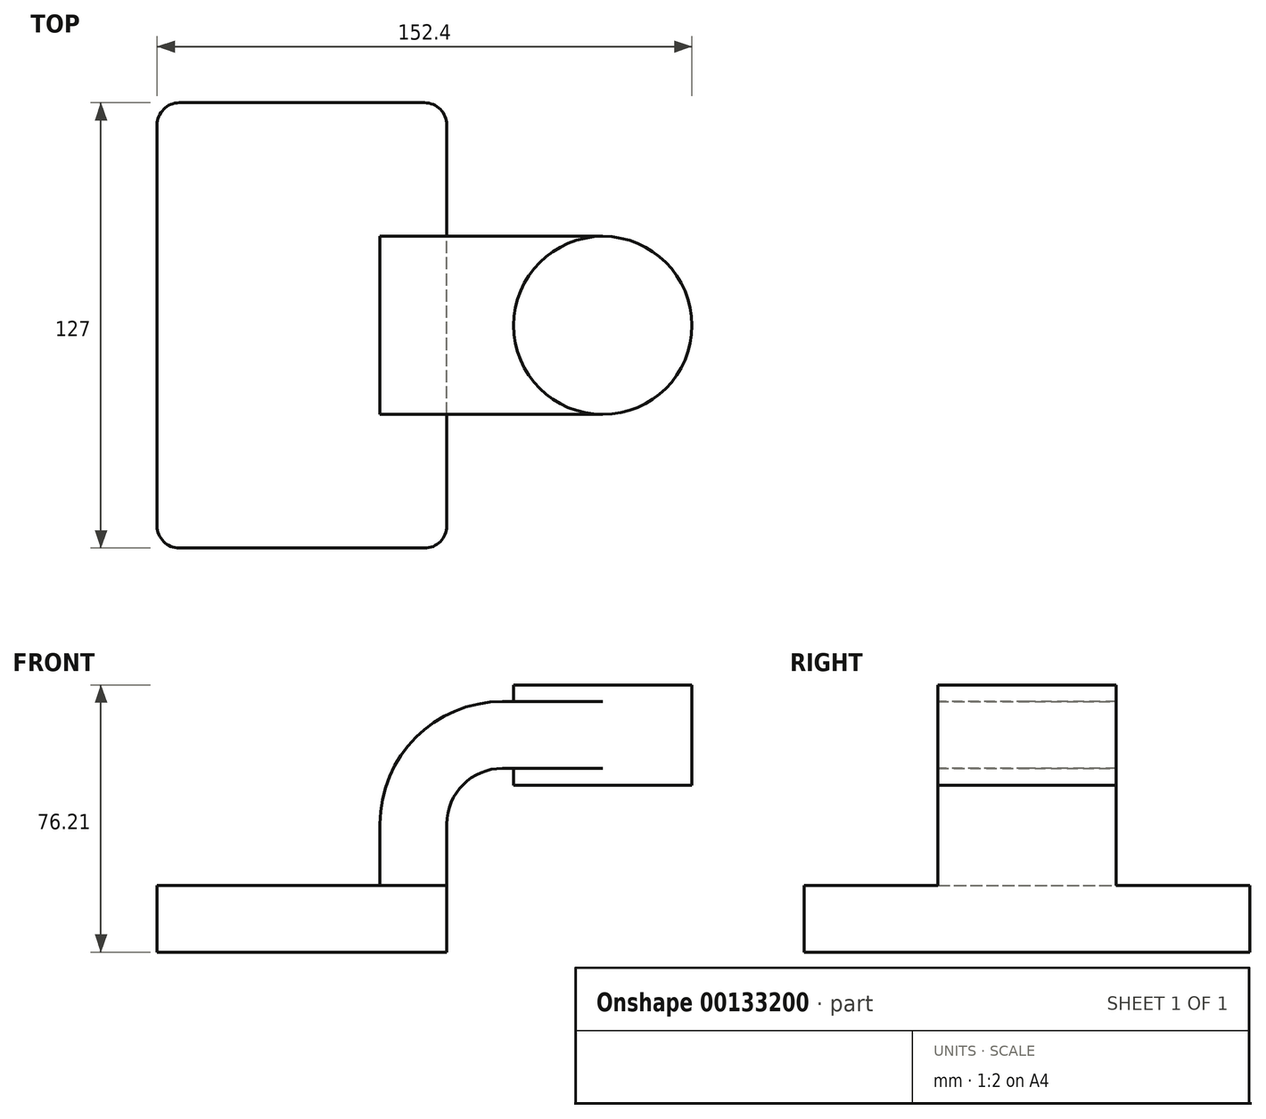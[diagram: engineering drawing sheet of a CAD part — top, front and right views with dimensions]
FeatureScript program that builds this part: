
annotation { "Feature Type Name" : "Feature", "Feature Type Description" : "" }
export const myFeature = defineFeature(function(context is Context, id is Id, definition is map)
    precondition{}
    {
        {
            var Q0;
            Q0=qCreatedBy(makeId("Front.planeOp"),FACE);
            var sketch = newSketch(context, id + "F0", { "sketchPlane" : qUnion([Q0])});
            skLineSegment(sketch, "E0.bottom", {"start": v(-41.28, -9.53) * mm, "end": v(41.28, -9.53) * mm});
            skLineSegment(sketch, "E0.top", {"start": v(-41.28, 9.53) * mm, "end": v(41.28, 9.53) * mm});
            skLineSegment(sketch, "E0.left", {"start": v(-41.28, -9.53) * mm, "end": v(-41.28, 9.53) * mm});
            skLineSegment(sketch, "E0.right", {"start": v(41.28, -9.53) * mm, "end": v(41.28, 9.52) * mm});
            skPoint(sketch, "E0.middle", {"position": v(0, 0) * mm});
            skLineSegment(sketch, "E1.bottom", {"start": v(60.32, 38.1) * mm, "end": v(111.12, 38.1) * mm});
            skLineSegment(sketch, "E1.top", {"start": v(60.32, 66.67) * mm, "end": v(111.12, 66.67) * mm});
            skLineSegment(sketch, "E1.left", {"start": v(60.32, 38.1) * mm, "end": v(60.32, 66.67) * mm});
            skLineSegment(sketch, "E1.right", {"start": v(111.12, 38.1) * mm, "end": v(111.12, 66.67) * mm});
            skPoint(sketch, "E1.middle", {"position": v(85.72, 52.39) * mm});
            skLineSegment(sketch, "E2", {"start": v(41.28, 9.52) * mm, "end": v(41.28, 27) * mm});
            skArc(sketch, "E3", {"start": v(41.27, 27) * mm, "mid": v(45.92, 38.23) * mm, "end": v(57.15, 42.88) * mm});
            skLineSegment(sketch, "E4", {"start": v(57.15, 42.88) * mm, "end": v(85.72, 42.88) * mm});
            skLineSegment(sketch, "E5.0", {"start": v(57.15, 61.93) * mm, "end": v(85.72, 61.93) * mm});
            skArc(sketch, "E5.1", {"start": v(22.22, 27) * mm, "mid": v(32.45, 51.7) * mm, "end": v(57.15, 61.93) * mm});
            skLineSegment(sketch, "E5.2", {"start": v(22.22, 9.52) * mm, "end": v(22.22, 27) * mm});
            skFitSpline(sketch, "E6", {"points": [v(-41.28, 9.53) * mm, v(57.15, 61.93) * mm], "startDerivative": vector(39.13, 103.02) * mm, "endDerivative": vector(111.96, -0.1) * mm});
            skLineSegment(sketch, "E7", {"start": v(85.72, 38.1) * mm, "end": v(85.72, 66.67) * mm});
            skSolve(sketch);
        }
        {
            var Q0;
            Q0=makeQuery(id+"F0.imprint","IMPRINT",FACE,{"disambiguationData":[TD([[makeQuery(id+"F0.imprint","IMPRINT",EDGE,{"derivedFrom":sQuery(id+"F0.wireOp",EDGE,"E0.bottom")}),1.0]])]});
            extrude(context, id + "F1", {"entities" : qUnion([Q0]), "endBound" : BoundingType.SYMMETRIC, "depth" : 127 * mm});
        }
        {
            var Q0;
            {var subQ1=sQuery(id+"F0.wireOp",EDGE,"E2");Q0=makeQuery(id+"F0.imprint","IMPRINT",FACE,{"disambiguationData":[TD([[makeQuery(id+"F0.imprint","IMPRINT",EDGE,{"derivedFrom":subQ1}),1.0]])]});}
            var Q1;
            {var subQ0=sQuery(id+"F0.wireOp",EDGE,"E4");var subQ1=sQuery(id+"F0.wireOp",EDGE,"E1.left");var subQ2=makeQuery(id+"F0.imprint","INTERSECT",VERTEX,{"derivedFrom":[subQ1,subQ0]});Q1=makeQuery(id+"F0.imprint","IMPRINT",FACE,{"disambiguationData":[TD([[makeQuery(id+"F0.imprint","IMPRINT",EDGE,{"disambiguationData":[TD([[subQ2,-1.0]])],"derivedFrom":subQ1}),-1.0]])]});}
            extrude(context, id + "F2", {"entities" : qUnion([Q0, Q1]), "operationType" : NewBodyOperationType.ADD, "endBound" : BoundingType.SYMMETRIC, "depth" : 50.8 * mm});
        }
        {
            var Q0;
            Q0=makeQuery(id+"F0.imprint","IMPRINT",FACE,{"disambiguationData":[TD([[makeQuery(id+"F0.imprint","IMPRINT",EDGE,{"derivedFrom":sQuery(id+"F0.wireOp",EDGE,"E5.1")}),1.0]])]});
            extrude(context, id + "F3", {"entities" : qUnion([Q0]), "operationType" : NewBodyOperationType.ADD, "endBound" : BoundingType.SYMMETRIC, "depth" : 15.88 * mm});
        }
        {
            var Q0;
            {var subQ0=sQuery(id+"F0.wireOp",EDGE,"E1.right");Q0=makeQuery(id+"F0.imprint","IMPRINT",FACE,{"disambiguationData":[TD([[makeQuery(id+"F0.imprint","IMPRINT",EDGE,{"derivedFrom":subQ0}),1.0]])]});}
            var Q1;
            Q1=sQuery(id+"F0.wireOp",EDGE,"E7");
            revolve(context, id + "F4", {"operationType" : NewBodyOperationType.ADD, "entities" : qUnion([Q0]), "axis" : qUnion([Q1]), "revolveType" : RevolveType.FULL});
        }
        {
            var Q0;
            Q0=makeQuery(id+"F1.opExtrude","CAP_EDGE",EDGE,{"disambiguationData":[OSD([sQuery(id+"F0.wireOp",EDGE,"E0.left")])],"isStart":false});
            var Q1;
            Q1=makeQuery(id+"F1.opExtrude","CAP_EDGE",EDGE,{"disambiguationData":[OSD([sQuery(id+"F0.wireOp",EDGE,"E0.right")])],"isStart":false});
            var Q2;
            Q2=makeQuery(id+"F1.opExtrude","CAP_EDGE",EDGE,{"disambiguationData":[OSD([sQuery(id+"F0.wireOp",EDGE,"E0.right")])],"isStart":true});
            var Q3;
            Q3=makeQuery(id+"F1.opExtrude","CAP_EDGE",EDGE,{"disambiguationData":[OSD([sQuery(id+"F0.wireOp",EDGE,"E0.left")])],"isStart":true});
            fillet(context, id + "F5", {"entities" : qUnion([Q0, Q1, Q2, Q3]), "radius" : 6.35 * mm, "tangentPropagation" : true, "allowEdgeOverflow" : false});
        }
    });
